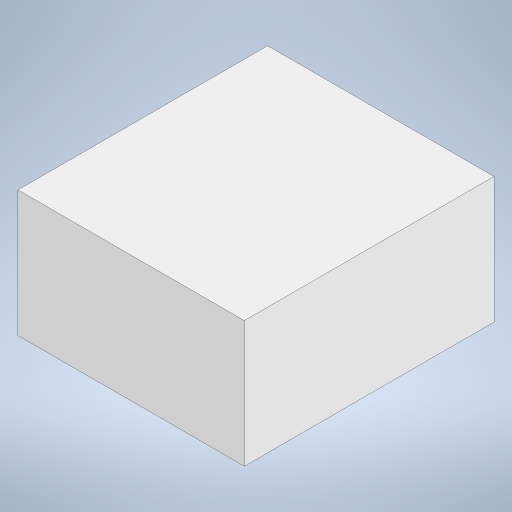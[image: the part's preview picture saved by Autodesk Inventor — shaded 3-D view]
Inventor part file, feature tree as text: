
AUTODESK INVENTOR PART (.ipt)
format: ipt  version: 2024 (Build 280153000, 153)  size: 166,912 bytes
history: native  units: in
note: dims shown in document units (in); Inventor stores cm internally (conversion verified against a paired STEP export)
features: extrude x1, sketch x1
ambient origin geometry x8: Origin, YZ Plane, XZ Plane, XY Plane, X Axis, Y Axis, Z Axis, Center Point
bodies: Solid1 (feature_tree)
feature tree (2):
  extrude  "Extrusion1"  Depth=9.65in
  sketch  "Sketch1"  dims[d1=19.1in d2=9.65in d3=17.32in d4=0.0in]
